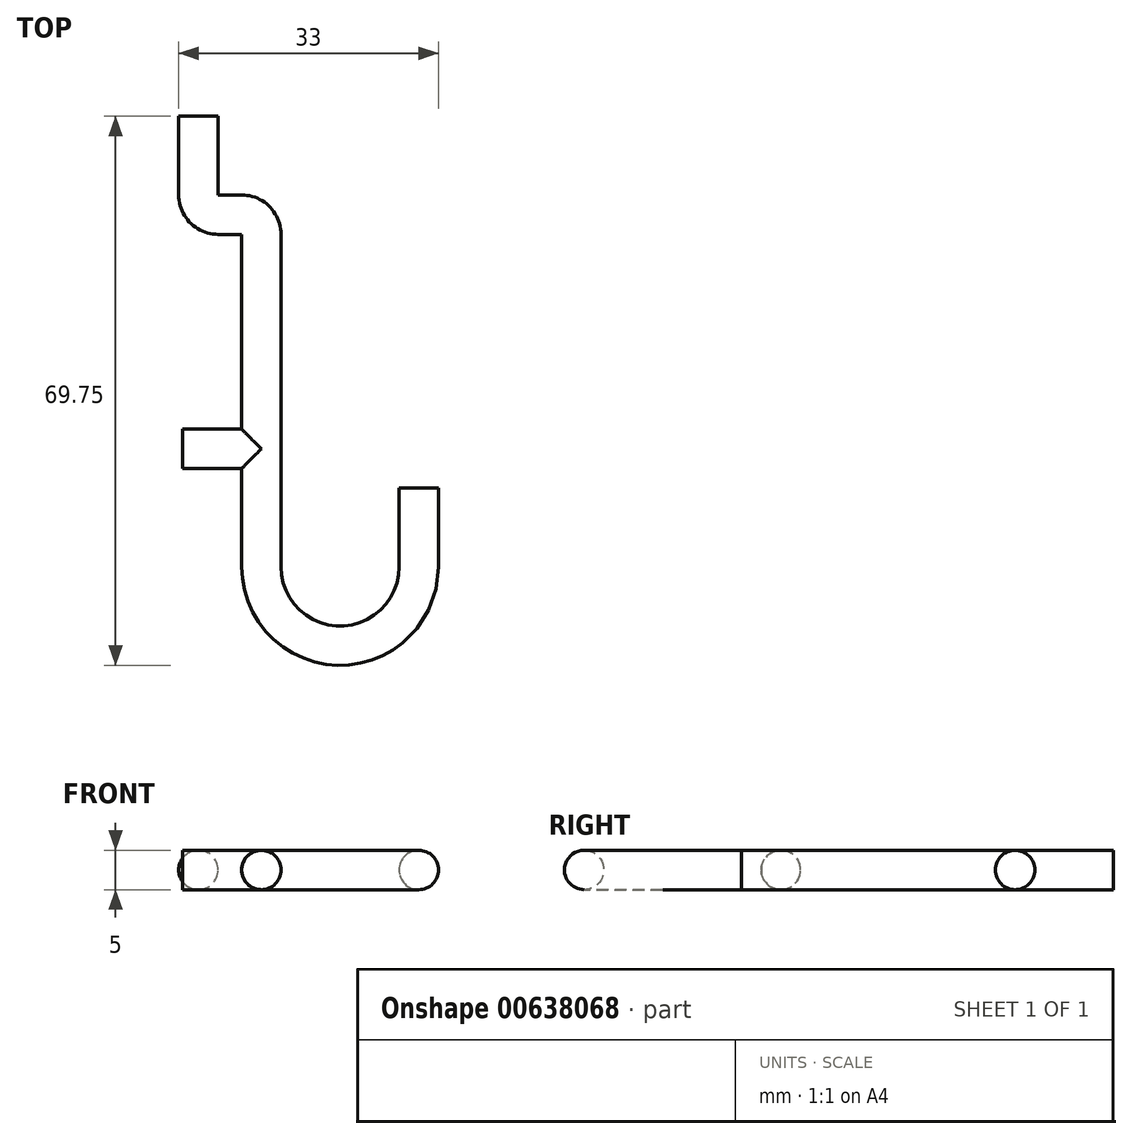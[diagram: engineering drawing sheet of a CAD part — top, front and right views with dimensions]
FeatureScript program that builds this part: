
annotation { "Feature Type Name" : "Feature", "Feature Type Description" : "" }
export const myFeature = defineFeature(function(context is Context, id is Id, definition is map)
    precondition{}
    {
        {
            var Q0;
            Q0=qCreatedBy(makeId("Top.planeOp"),FACE);
            var sketch = newSketch(context, id + "F0", { "sketchPlane" : qUnion([Q0])});
            skLineSegment(sketch, "E0", {"start": v(0, 0) * mm, "end": v(0, 27.25) * mm});
            skArc(sketch, "E1", {"start": v(0, 27.25) * mm, "mid": v(-0.73, 29.02) * mm, "end": v(-2.5, 29.75) * mm});
            skLineSegment(sketch, "E2", {"start": v(-2.5, 29.75) * mm, "end": v(-5.5, 29.75) * mm});
            skArc(sketch, "E3", {"start": v(-5.5, 29.75) * mm, "mid": v(-7.27, 30.48) * mm, "end": v(-8, 32.25) * mm});
            skLineSegment(sketch, "E4", {"start": v(-8, 32.25) * mm, "end": v(-8, 42.25) * mm});
            skLineSegment(sketch, "E5", {"start": v(0, 0) * mm, "end": v(0, -15) * mm});
            skArc(sketch, "E6", {"start": v(0, -15) * mm, "mid": v(10, -25) * mm, "end": v(20, -15) * mm});
            skLineSegment(sketch, "E7", {"start": v(20, -15) * mm, "end": v(20, -5) * mm});
            skSolve(sketch);
        }
        {
            var Q0;
            Q0=qCreatedBy(makeId("Front.planeOp"),FACE);
            cPlane(context, id + "F1", {"entities" : qUnion([Q0]), "cplaneType" : CPlaneType.OFFSET, "offset" : 5 * mm, "width" : 150 * mm, "height" : 150 * mm});
        }
        {
            var Q0;
            Q0=qCreatedBy(id+"F1.planeOp",FACE);
            var sketch = newSketch(context, id + "F2", { "sketchPlane" : qUnion([Q0])});
            skCircle(sketch, "E8", {"center": v(20, 0) * mm, "radius": 2.5 * mm});
            skSolve(sketch);
        }
        {
            var Q0;
            Q0=makeQuery(id+"F2.imprint","IMPRINT",FACE,{"disambiguationData":[TD([[makeQuery(id+"F2.imprint","IMPRINT",EDGE,{"derivedFrom":sQuery(id+"F2.wireOp",EDGE,"E8")}),1.0]])]});
            var Q1;
            Q1=sQuery(id+"F0.wireOp",EDGE,"E7");
            var Q2;
            Q2=sQuery(id+"F0.wireOp",EDGE,"E6");
            var Q3;
            Q3=sQuery(id+"F0.wireOp",EDGE,"E5");
            var Q4;
            Q4=sQuery(id+"F0.wireOp",EDGE,"E0");
            var Q5;
            Q5=sQuery(id+"F0.wireOp",EDGE,"E1");
            var Q6;
            Q6=sQuery(id+"F0.wireOp",EDGE,"E2");
            var Q7;
            Q7=sQuery(id+"F0.wireOp",EDGE,"E3");
            var Q8;
            Q8=sQuery(id+"F0.wireOp",EDGE,"E4");
            sweep(context, id + "F3", {"profiles" : qUnion([Q0]), "path" : qUnion([Q1, Q2, Q3, Q4, Q5, Q6, Q7, Q8])});
        }
        {
            var Q0;
            Q0=qCreatedBy(makeId("Top.planeOp"),FACE);
            var sketch = newSketch(context, id + "F4", { "sketchPlane" : qUnion([Q0])});
            skLineSegment(sketch, "E9", {"start": v(0, 0) * mm, "end": v(-10, 0) * mm});
            skSolve(sketch);
        }
        {
            var Q0;
            Q0=qCreatedBy(makeId("Right.planeOp"),FACE);
            var sketch = newSketch(context, id + "F5", { "sketchPlane" : qUnion([Q0])});
            skCircle(sketch, "E10", {"center": v(0, 0) * mm, "radius": 2.5 * mm});
            skSolve(sketch);
        }
        {
            var Q0;
            Q0 = qSketchRegion(id + "F5", true);
            var Q1;
            Q1=sQuery(id+"F4.wireOp",EDGE,"E9");
            sweep(context, id + "F6", {"operationType" : NewBodyOperationType.ADD, "profiles" : qUnion([Q0]), "path" : qUnion([Q1])});
        }
    });
